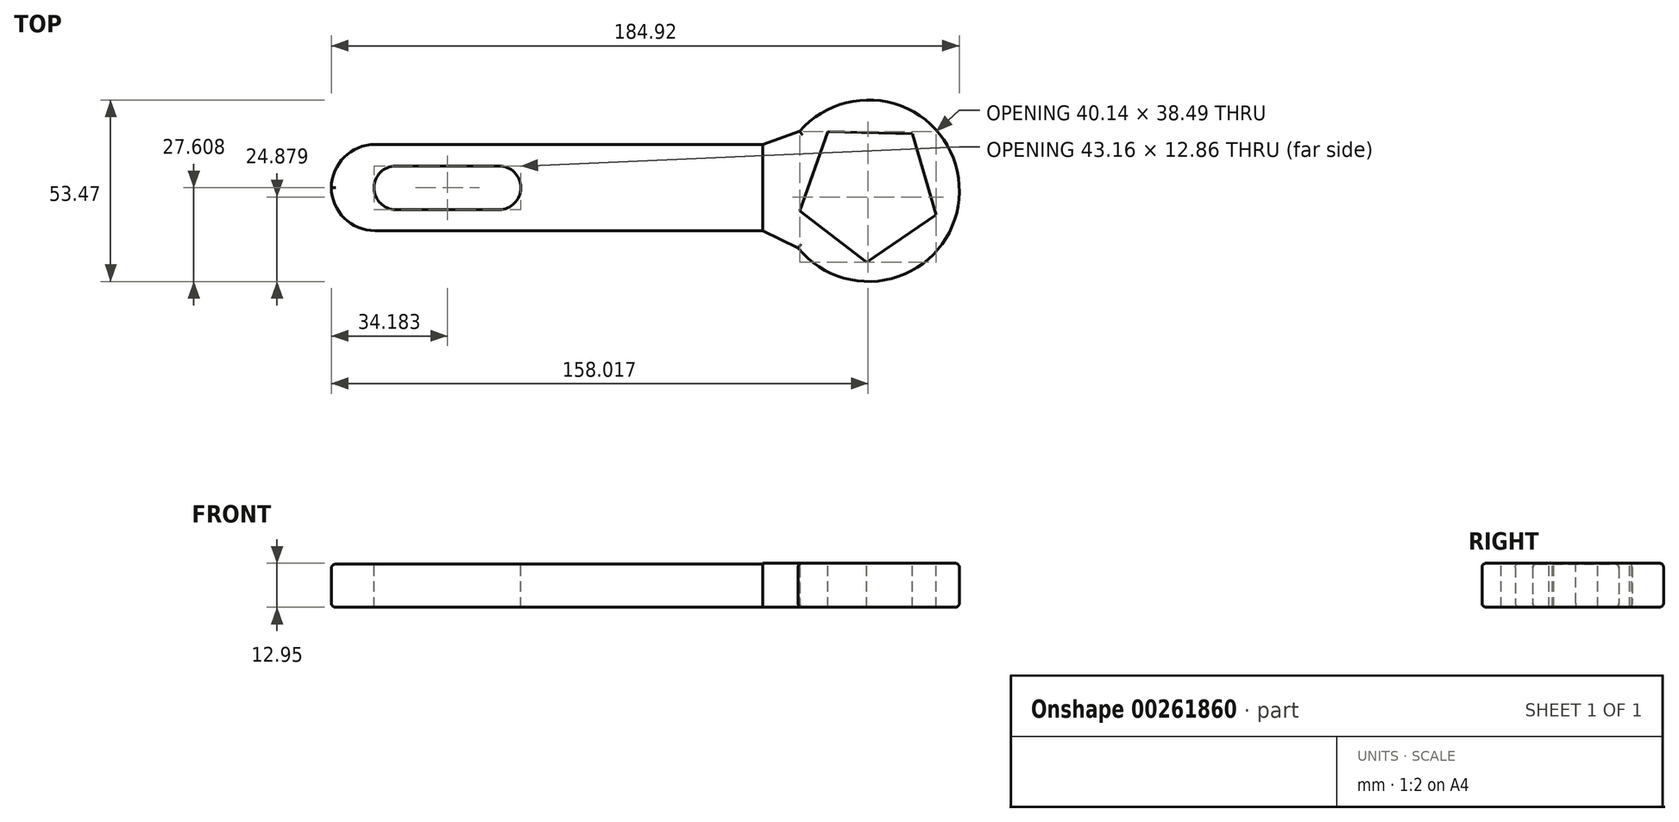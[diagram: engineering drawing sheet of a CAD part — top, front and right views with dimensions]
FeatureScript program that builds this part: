
annotation { "Feature Type Name" : "Feature", "Feature Type Description" : "" }
export const myFeature = defineFeature(function(context is Context, id is Id, definition is map)
    precondition{}
    {
        {
            var Q0;
            Q0=qCreatedBy(makeId("Front.planeOp"),FACE);
            var sketch = newSketch(context, id + "F0", { "sketchPlane" : qUnion([Q0])});
            skLineSegment(sketch, "E0", {"start": v(0, 0) * mm, "end": v(-60.67, 0) * mm});
            skLineSegment(sketch, "E1", {"start": v(-60.67, 0) * mm, "end": v(66.33, 0) * mm});
            skLineSegment(sketch, "E2", {"start": v(66.33, 0) * mm, "end": v(66.33, 10.69) * mm});
            skLineSegment(sketch, "E3", {"start": v(-60.67, 0) * mm, "end": v(-60.67, 12.7) * mm});
            skLineSegment(sketch, "E4", {"start": v(-60.67, 12.7) * mm, "end": v(66.34, 12.7) * mm});
            skLineSegment(sketch, "E5", {"start": v(66.34, 12.7) * mm, "end": v(66.33, 0) * mm});
            skSolve(sketch);
        }
        {
            var Q0;
            {var subQ0=sQuery(id+"F0.wireOp",EDGE,"E3");Q0=makeQuery(id+"F0.imprint","IMPRINT",FACE,{"disambiguationData":[TD([[makeQuery(id+"F0.imprint","IMPRINT",EDGE,{"derivedFrom":subQ0}),-1.0]])]});}
            extrude(context, id + "F1", {"entities" : qUnion([Q0]), "depth" : 25.4 * mm});
        }
        {
            var Q0;
            Q0=makeQuery(id+"F1.opExtrude","CAP_EDGE",EDGE,{"disambiguationData":[OSD([sQuery(id+"F0.wireOp",EDGE,"E3")])],"isStart":false});
            var Q1;
            Q1=makeQuery(id+"F1.opExtrude","CAP_EDGE",EDGE,{"disambiguationData":[OSD([sQuery(id+"F0.wireOp",EDGE,"E3")])],"isStart":true});
            fillet(context, id + "F2", {"entities" : qUnion([Q0, Q1]), "radius" : 12.88 * mm, "tangentPropagation" : true, "allowEdgeOverflow" : false});
        }
        {
            var Q0;
            Q0=makeQuery(id+"F1.opExtrude","SWEPT_FACE",FACE,{"disambiguationData":[OSD([sQuery(id+"F0.wireOp",EDGE,"E4")])]});
            var sketch = newSketch(context, id + "F3", { "sketchPlane" : qUnion([Q0])});
            skLineSegment(sketch, "E6", {"start": v(66.34, -25.4) * mm, "end": v(76.77, -30.49) * mm});
            skCircle(sketch, "E7", {"center": v(97.52, -13.62) * mm, "radius": 26.74 * mm});
            skPoint(sketch, "E7.second.point", {"position": v(124.23, -12.52) * mm});
            skPoint(sketch, "E7.third.point", {"position": v(119.37, -29.02) * mm});
            skLineSegment(sketch, "E8", {"start": v(66.34, 0) * mm, "end": v(77.29, 3.87) * mm});
            skSolve(sketch);
        }
        {
            var Q0;
            Q0 = qSketchRegion(id + "F3", true);
            var Q1;
            {var subQ0=sQuery(id+"F3.wireOp",EDGE,"E6");Q1=makeQuery(id+"F3.imprint","IMPRINT",FACE,{"disambiguationData":[TD([[makeQuery(id+"F3.imprint","IMPRINT",EDGE,{"derivedFrom":subQ0}),1.0]])]});}
            extrude(context, id + "F4", {"entities" : qUnion([Q0, Q1]), "depth" : 0.25 * mm, "hasSecondDirection" : true, "secondDirectionOppositeDirection" : true, "secondDirectionDepth" : 12.7 * mm});
        }
        {
            var Q0;
            Q0=makeQuery(id+"F4.opExtrude","CAP_FACE",FACE,{"disambiguationData":[OSD([sQuery(id+"F0.wireOp",EDGE,"E4"),sQuery(id+"F0.wireOp",EDGE,"E5"),sQuery(id+"F3.wireOp",EDGE,"E6"),sQuery(id+"F3.wireOp",EDGE,"E7"),sQuery(id+"F3.wireOp",EDGE,"E8")])],"isStart":false});
            var sketch = newSketch(context, id + "F5", { "sketchPlane" : qUnion([Q0])});
            skCircle(sketch, "E9.cCircle", {"center": v(97.52, -13.62) * mm, "radius": 17.08 * mm, "construction": true});
            skLineSegment(sketch, "E9.0", {"start": v(77.28, -19.62) * mm, "end": v(85.56, 3.78) * mm});
            skLineSegment(sketch, "E9.1", {"start": v(85.56, 3.78) * mm, "end": v(110.36, 3.13) * mm});
            skLineSegment(sketch, "E9.2", {"start": v(110.36, 3.13) * mm, "end": v(117.42, -20.66) * mm});
            skLineSegment(sketch, "E9.3", {"start": v(117.42, -20.66) * mm, "end": v(96.97, -34.72) * mm});
            skLineSegment(sketch, "E9.4", {"start": v(96.97, -34.72) * mm, "end": v(77.28, -19.62) * mm});
            skPoint(sketch, "E9.0.midPoint", {"position": v(81.42, -7.92) * mm});
            skSolve(sketch);
        }
        {
            var Q0;
            Q0 = qSketchRegion(id + "F5", true);
            extrude(context, id + "F6", {"entities" : qUnion([Q0]), "operationType" : NewBodyOperationType.REMOVE, "oppositeDirection" : true, "depth" : 25.4 * mm});
        }
        {
            var Q0;
            Q0=makeQuery(id+"F1.opExtrude","SWEPT_FACE",FACE,{"disambiguationData":[OSD([sQuery(id+"F0.wireOp",EDGE,"E4")])]});
            var sketch = newSketch(context, id + "F7", { "sketchPlane" : qUnion([Q0])});
            skLineSegment(sketch, "E10.bottom", {"start": v(-41.72, -19.17) * mm, "end": v(-11.26, -19.17) * mm});
            skLineSegment(sketch, "E10.top", {"start": v(-41.72, -6.31) * mm, "end": v(-11.26, -6.31) * mm});
            skLineSegment(sketch, "E10.left", {"start": v(-48.07, -12.82) * mm, "end": v(-48.07, -12.66) * mm});
            skLineSegment(sketch, "E10.right", {"start": v(-4.9, -12.82) * mm, "end": v(-4.9, -12.66) * mm});
            skPoint(sketch, "E11.visualSharp", {"position": v(-48.07, -6.31) * mm});
            skArc(sketch, "E11.filletArc", {"start": v(-41.72, -6.31) * mm, "mid": v(-46.2, -8.17) * mm, "end": v(-48.07, -12.66) * mm});
            skPoint(sketch, "E12.visualSharp", {"position": v(-48.07, -19.17) * mm});
            skArc(sketch, "E12.filletArc", {"start": v(-48.07, -12.82) * mm, "mid": v(-46.2, -17.31) * mm, "end": v(-41.72, -19.17) * mm});
            skPoint(sketch, "E13.visualSharp", {"position": v(-4.9, -19.17) * mm});
            skArc(sketch, "E13.filletArc", {"start": v(-11.26, -19.17) * mm, "mid": v(-6.77, -17.31) * mm, "end": v(-4.9, -12.82) * mm});
            skPoint(sketch, "E14.visualSharp", {"position": v(-4.9, -6.31) * mm});
            skArc(sketch, "E14.filletArc", {"start": v(-4.9, -12.66) * mm, "mid": v(-6.77, -8.17) * mm, "end": v(-11.26, -6.31) * mm});
            skSolve(sketch);
        }
        {
            var Q0;
            Q0=makeQuery(id+"F7.imprint","IMPRINT",FACE,{"disambiguationData":[TD([[makeQuery(id+"F7.imprint","IMPRINT",EDGE,{"derivedFrom":sQuery(id+"F7.wireOp",EDGE,"E10.bottom")}),1.0]])]});
            extrude(context, id + "F8", {"entities" : qUnion([Q0]), "operationType" : NewBodyOperationType.REMOVE, "oppositeDirection" : true, "depth" : 25.4 * mm});
        }
        {
            var Q0;
            Q0=makeQuery(id+"F2.opFillet","BLEND_EDGE",EDGE,{"blendedFrom":[makeQuery(id+"F1.opExtrude","CAP_EDGE",EDGE,{"disambiguationData":[OSD([sQuery(id+"F0.wireOp",EDGE,"E3")])],"isStart":false}),makeQuery(id+"F1.opExtrude","SWEPT_FACE",FACE,{"disambiguationData":[OSD([sQuery(id+"F0.wireOp",EDGE,"E4")])]})],"blendedInto":[makeQuery(id+"F1.opExtrude","SWEPT_FACE",FACE,{"disambiguationData":[OSD([sQuery(id+"F0.wireOp",EDGE,"E4")])]})]});
            var Q1;
            Q1=makeQuery(id+"F2.opFillet","BLEND_EDGE",EDGE,{"blendedFrom":[makeQuery(id+"F1.opExtrude","CAP_EDGE",EDGE,{"disambiguationData":[OSD([sQuery(id+"F0.wireOp",EDGE,"E3")])],"isStart":true}),makeQuery(id+"F1.opExtrude","SWEPT_FACE",FACE,{"disambiguationData":[OSD([sQuery(id+"F0.wireOp",EDGE,"E4")])]})],"blendedInto":[makeQuery(id+"F1.opExtrude","SWEPT_FACE",FACE,{"disambiguationData":[OSD([sQuery(id+"F0.wireOp",EDGE,"E4")])]})]});
            var Q2;
            Q2=makeQuery(id+"F1.opExtrude","CAP_EDGE",EDGE,{"disambiguationData":[OSD([sQuery(id+"F0.wireOp",EDGE,"E4")])],"isStart":false});
            var Q3;
            Q3=makeQuery(id+"F1.opExtrude","CAP_EDGE",EDGE,{"disambiguationData":[OSD([sQuery(id+"F0.wireOp",EDGE,"E4")])],"isStart":true});
            var Q4;
            Q4=makeQuery(id+"F4.opExtrude","CAP_EDGE",EDGE,{"disambiguationData":[OSD([sQuery(id+"F3.wireOp",EDGE,"E6")])],"isStart":false});
            var Q5;
            Q5=makeQuery(id+"F4.opExtrude","CAP_EDGE",EDGE,{"disambiguationData":[OSD([sQuery(id+"F3.wireOp",EDGE,"E8")])],"isStart":false});
            var Q6;
            Q6=makeQuery(id+"F4.opExtrude","CAP_EDGE",EDGE,{"disambiguationData":[OSD([sQuery(id+"F3.wireOp",EDGE,"E7")])],"isStart":false});
            var Q7;
            Q7=makeQuery(id+"F1.opExtrude","CAP_EDGE",EDGE,{"disambiguationData":[OSD([sQuery(id+"F0.wireOp",EDGE,"E1")])],"isStart":false});
            var Q8;
            Q8=makeQuery(id+"F2.opFillet","BLEND_EDGE",EDGE,{"blendedFrom":[makeQuery(id+"F1.opExtrude","CAP_EDGE",EDGE,{"disambiguationData":[OSD([sQuery(id+"F0.wireOp",EDGE,"E3")])],"isStart":true}),makeQuery(id+"F1.opExtrude","SWEPT_FACE",FACE,{"disambiguationData":[OSD([sQuery(id+"F0.wireOp",EDGE,"E1")])]})],"blendedInto":[makeQuery(id+"F1.opExtrude","SWEPT_FACE",FACE,{"disambiguationData":[OSD([sQuery(id+"F0.wireOp",EDGE,"E1")])]})]});
            var Q9;
            Q9=makeQuery(id+"F2.opFillet","BLEND_EDGE",EDGE,{"blendedFrom":[makeQuery(id+"F1.opExtrude","CAP_EDGE",EDGE,{"disambiguationData":[OSD([sQuery(id+"F0.wireOp",EDGE,"E3")])],"isStart":false}),makeQuery(id+"F1.opExtrude","SWEPT_FACE",FACE,{"disambiguationData":[OSD([sQuery(id+"F0.wireOp",EDGE,"E1")])]})],"blendedInto":[makeQuery(id+"F1.opExtrude","SWEPT_FACE",FACE,{"disambiguationData":[OSD([sQuery(id+"F0.wireOp",EDGE,"E1")])]})]});
            var Q10;
            Q10=makeQuery(id+"F1.opExtrude","CAP_EDGE",EDGE,{"disambiguationData":[OSD([sQuery(id+"F0.wireOp",EDGE,"E1")])],"isStart":true});
            var Q11;
            Q11=makeQuery(id+"F4.opExtrude","CAP_EDGE",EDGE,{"disambiguationData":[OSD([sQuery(id+"F3.wireOp",EDGE,"E6")])],"isStart":true});
            var Q12;
            Q12=makeQuery(id+"F4.opExtrude","CAP_EDGE",EDGE,{"disambiguationData":[OSD([sQuery(id+"F3.wireOp",EDGE,"E8")])],"isStart":true});
            var Q13;
            Q13=makeQuery(id+"F4.opExtrude","CAP_EDGE",EDGE,{"disambiguationData":[OSD([sQuery(id+"F3.wireOp",EDGE,"E7")])],"isStart":true});
            fillet(context, id + "F9", {"entities" : qUnion([Q0, Q1, Q2, Q3, Q4, Q5, Q6, Q7, Q8, Q9, Q10, Q11, Q12, Q13]), "radius" : 1.23 * mm, "tangentPropagation" : true, "allowEdgeOverflow" : false});
        }
    });
